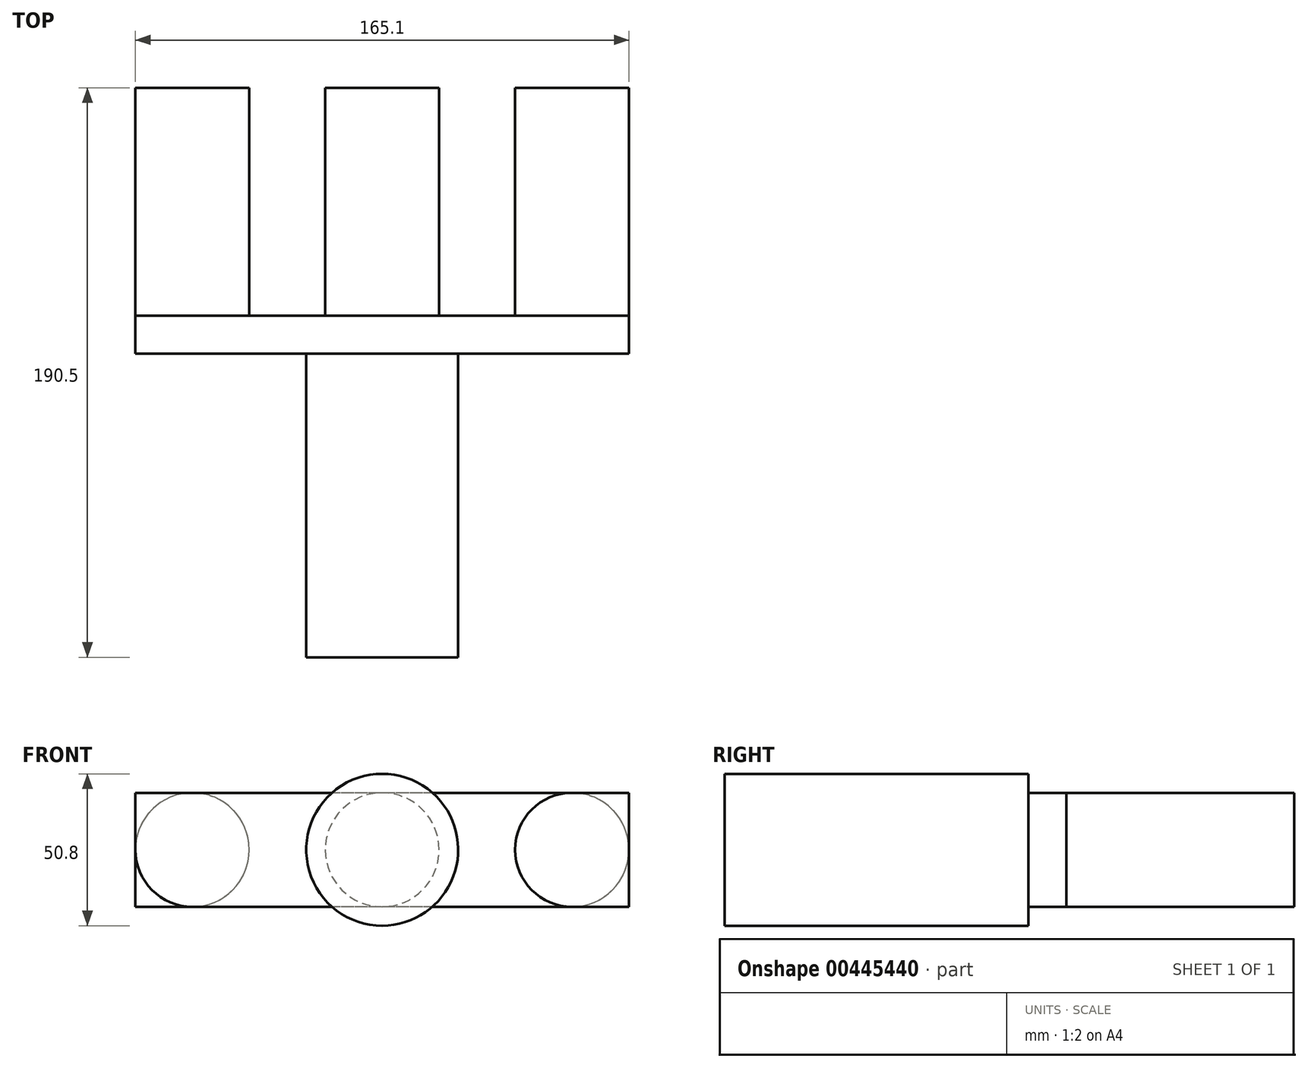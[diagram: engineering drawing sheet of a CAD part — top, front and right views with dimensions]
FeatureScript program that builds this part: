
annotation { "Feature Type Name" : "Feature", "Feature Type Description" : "" }
export const myFeature = defineFeature(function(context is Context, id is Id, definition is map)
    precondition{}
    {
        {
            var Q0;
            Q0=qCreatedBy(makeId("Front.planeOp"),FACE);
            var sketch = newSketch(context, id + "F0", { "sketchPlane" : qUnion([Q0])});
            skCircle(sketch, "E0", {"center": v(0, 0) * mm, "radius": 19.05 * mm});
            skLineSegment(sketch, "E1", {"start": v(0, 0) * mm, "end": v(-63.5, 0) * mm});
            skCircle(sketch, "E2", {"center": v(-63.5, 0) * mm, "radius": 19.05 * mm});
            skLineSegment(sketch, "E3", {"start": v(0, 0) * mm, "end": v(63.5, 0) * mm});
            skCircle(sketch, "E4", {"center": v(63.5, 0) * mm, "radius": 19.05 * mm});
            skSolve(sketch);
        }
        {
            var Q0;
            Q0 = qSketchRegion(id + "F0", true);
            extrude(context, id + "F1", {"entities" : qUnion([Q0]), "depth" : 76.2 * mm});
        }
        {
            var Q0;
            Q0=makeQuery(id+"F1.opExtrude","CAP_FACE",FACE,{"disambiguationData":[OSD([sQuery(id+"F0.wireOp",EDGE,"E0")])],"isStart":false});
            var sketch = newSketch(context, id + "F2", { "sketchPlane" : qUnion([Q0])});
            skLineSegment(sketch, "E5.bottom", {"start": v(82.55, 19.05) * mm, "end": v(-82.55, 19.05) * mm});
            skLineSegment(sketch, "E5.top", {"start": v(82.55, -19.05) * mm, "end": v(-82.55, -19.05) * mm});
            skLineSegment(sketch, "E5.left", {"start": v(82.55, 19.05) * mm, "end": v(82.55, -19.05) * mm});
            skLineSegment(sketch, "E5.right", {"start": v(-82.55, 19.05) * mm, "end": v(-82.55, -19.05) * mm});
            skPoint(sketch, "E5.middle", {"position": v(0, 0) * mm});
            skSolve(sketch);
        }
        {
            var Q0;
            Q0 = qSketchRegion(id + "F2", true);
            extrude(context, id + "F3", {"entities" : qUnion([Q0]), "depth" : 12.7 * mm});
        }
        {
            var Q0;
            Q0=makeQuery(id+"F3.opExtrude","CAP_FACE",FACE,{"disambiguationData":[OSD([sQuery(id+"F2.wireOp",EDGE,"E5.bottom"),sQuery(id+"F2.wireOp",EDGE,"E5.top"),sQuery(id+"F2.wireOp",EDGE,"E5.left"),sQuery(id+"F2.wireOp",EDGE,"E5.right")])],"isStart":false});
            var sketch = newSketch(context, id + "F4", { "sketchPlane" : qUnion([Q0])});
            skCircle(sketch, "E6", {"center": v(0, 0) * mm, "radius": 25.4 * mm});
            skSolve(sketch);
        }
        {
            var Q0;
            Q0 = qSketchRegion(id + "F4", true);
            extrude(context, id + "F5", {"entities" : qUnion([Q0]), "operationType" : NewBodyOperationType.ADD, "depth" : 101.6 * mm});
        }
    });
